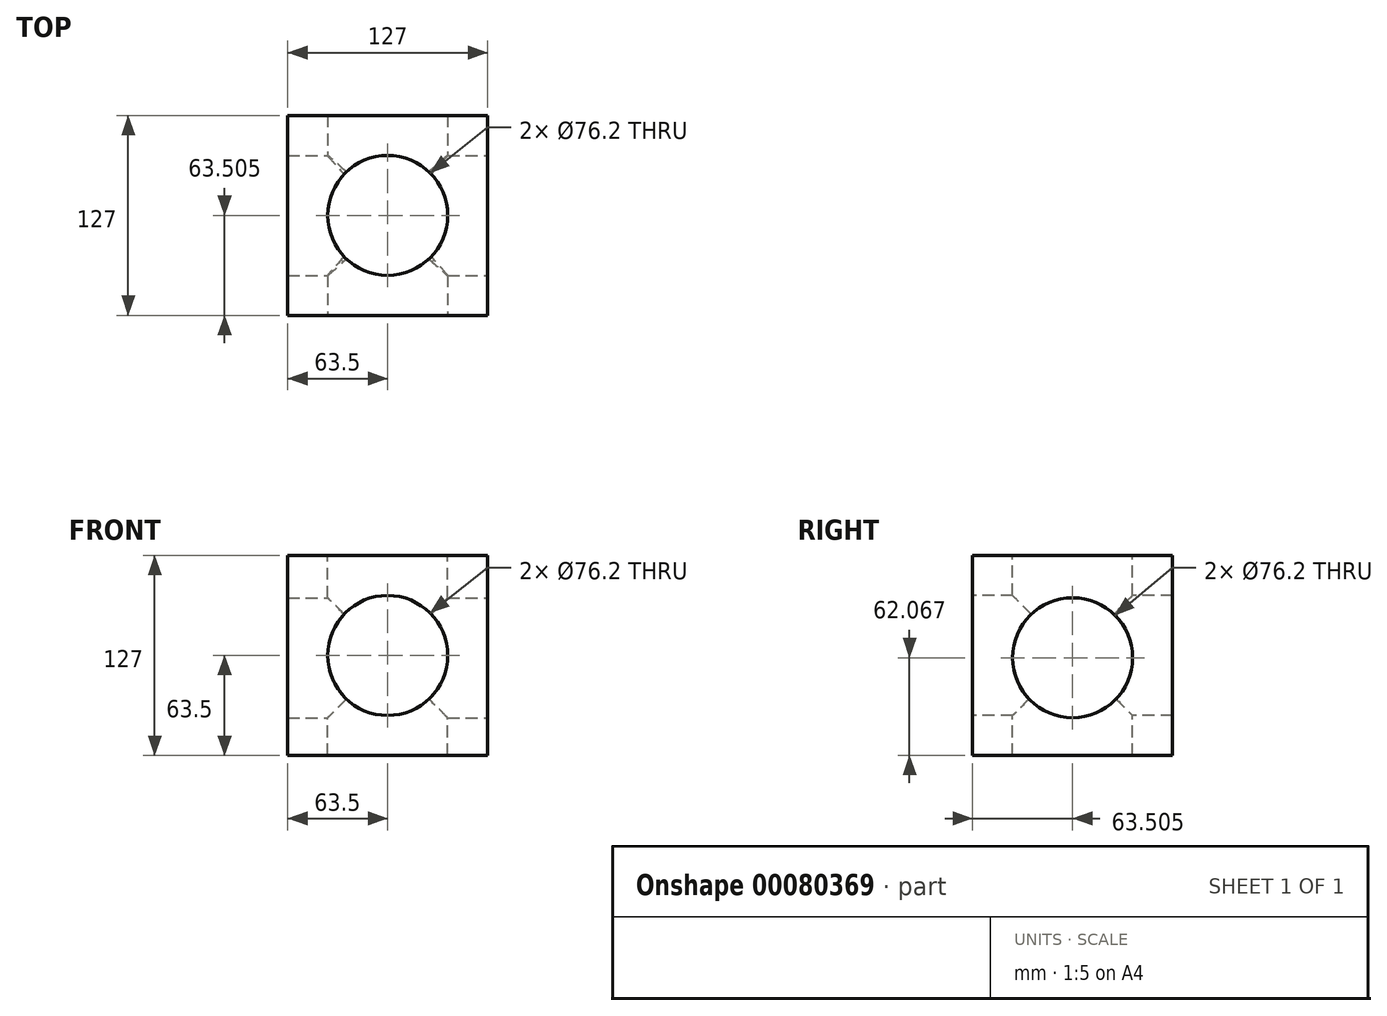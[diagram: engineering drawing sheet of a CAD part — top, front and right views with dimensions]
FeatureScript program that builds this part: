
annotation { "Feature Type Name" : "Feature", "Feature Type Description" : "" }
export const myFeature = defineFeature(function(context is Context, id is Id, definition is map)
    precondition{}
    {
        {
            var Q0;
            Q0=qCreatedBy(makeId("Top.planeOp"),FACE);
            var sketch = newSketch(context, id + "F0", { "sketchPlane" : qUnion([Q0])});
            skLineSegment(sketch, "E0.bottom", {"start": v(-56.96, 70.2) * mm, "end": v(70.04, 70.2) * mm});
            skLineSegment(sketch, "E0.top", {"start": v(-56.96, -56.8) * mm, "end": v(70.04, -56.8) * mm});
            skLineSegment(sketch, "E0.left", {"start": v(-56.96, 70.2) * mm, "end": v(-56.96, -56.8) * mm});
            skLineSegment(sketch, "E0.right", {"start": v(70.04, 70.2) * mm, "end": v(70.04, -56.8) * mm});
            skSolve(sketch);
        }
        {
            var Q0;
            Q0 = qSketchRegion(id + "F0", true);
            extrude(context, id + "F1", {"entities" : qUnion([Q0]), "depth" : 127 * mm});
        }
        {
            var Q0;
            Q0=makeQuery(id+"F1.opExtrude","CAP_FACE",FACE,{"disambiguationData":[OSD([sQuery(id+"F0.wireOp",EDGE,"E0.bottom"),sQuery(id+"F0.wireOp",EDGE,"E0.top"),sQuery(id+"F0.wireOp",EDGE,"E0.left"),sQuery(id+"F0.wireOp",EDGE,"E0.right")])],"isStart":false});
            var sketch = newSketch(context, id + "F2", { "sketchPlane" : qUnion([Q0])});
            skLineSegment(sketch, "E1", {"start": v(-56.96, 70.2) * mm, "end": v(70.04, -56.8) * mm, "construction": true});
            skCircle(sketch, "E2", {"center": v(6.54, 6.7) * mm, "radius": 38.1 * mm});
            skSolve(sketch);
        }
        {
            var Q0;
            Q0 = qSketchRegion(id + "F2", true);
            extrude(context, id + "F3", {"entities" : qUnion([Q0]), "operationType" : NewBodyOperationType.REMOVE, "endBound" : BoundingType.THROUGH_ALL, "oppositeDirection" : true, "depth" : 25.4 * mm});
        }
        {
            var Q0;
            Q0=makeQuery(id+"F1.opExtrude","SWEPT_FACE",FACE,{"disambiguationData":[OSD([sQuery(id+"F0.wireOp",EDGE,"E0.right")])]});
            var sketch = newSketch(context, id + "F4", { "sketchPlane" : qUnion([Q0])});
            skLineSegment(sketch, "E3", {"start": v(-56.8, 124.13) * mm, "end": v(70.2, 0) * mm, "construction": true});
            skCircle(sketch, "E4", {"center": v(6.7, 62.07) * mm, "radius": 38.1 * mm});
            skSolve(sketch);
        }
        {
            var Q0;
            Q0 = qSketchRegion(id + "F4", true);
            extrude(context, id + "F5", {"entities" : qUnion([Q0]), "operationType" : NewBodyOperationType.REMOVE, "endBound" : BoundingType.THROUGH_ALL, "oppositeDirection" : true, "depth" : 25.4 * mm});
        }
        {
            var Q0;
            Q0=makeQuery(id+"F1.opExtrude","SWEPT_FACE",FACE,{"disambiguationData":[OSD([sQuery(id+"F0.wireOp",EDGE,"E0.top")])]});
            var sketch = newSketch(context, id + "F6", { "sketchPlane" : qUnion([Q0])});
            skLineSegment(sketch, "E5", {"start": v(-56.96, 127) * mm, "end": v(70.04, 0) * mm, "construction": true});
            skCircle(sketch, "E6", {"center": v(6.54, 63.5) * mm, "radius": 38.1 * mm});
            skSolve(sketch);
        }
        {
            var Q0;
            Q0 = qSketchRegion(id + "F6", true);
            extrude(context, id + "F7", {"entities" : qUnion([Q0]), "operationType" : NewBodyOperationType.REMOVE, "endBound" : BoundingType.THROUGH_ALL, "oppositeDirection" : true, "depth" : 25.4 * mm});
        }
    });
